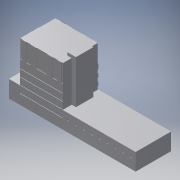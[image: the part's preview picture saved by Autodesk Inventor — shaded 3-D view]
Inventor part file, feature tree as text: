
AUTODESK INVENTOR PART (.ipt)
format: ipt  version: 2018.3 (Build 223284000, 284)  size: 415,744 bytes
history: native  units: mm
features: extrude x17, sketch x17, pattern_linear x3
ambient origin geometry x8: Origin, YZ Plane, XZ Plane, XY Plane, X Axis, Y Axis, Z Axis, Center Point
bodies: Solid1 (feature_tree)
feature tree (37):
  extrude  "Extrusion1"  Depth=28.01mm
  extrude  "Extrusion2"  Depth=0.31mm
  extrude  "Extrusion3"  Depth=8.81mm
  extrude  "Extrusion4"  Depth=33.64mm
  extrude  "Extrusion5"  Depth=31.92mm TaperAngle=0.0deg
  pattern_linear  "Rectangular Pattern1"  Count1=9 Spacing1=6.25mm
  extrude  "Extrusion6"  Depth=33.96mm
  extrude  "Extrusion7"  Depth=3.13mm
  pattern_linear  "Rectangular Pattern2"  Spacing1=7.78mm  [1 undecoded]
  extrude  "Extrusion8"  Depth=0.31mm TaperAngle=0.0deg
  extrude  "Extrusion9"  Depth=0.31mm TaperAngle=0.0deg
  extrude  "Extrusion10"  Depth=6.25mm
  extrude  "Extrusion11"  Depth=0.31mm TaperAngle=0.0deg
  pattern_linear  "Rectangular Pattern3"  Spacing1=5.26mm  [1 undecoded]
  extrude  "Extrusion12"  Depth=26.61mm
  extrude  "Extrusion13"  Depth=2.59mm
  extrude  "Extrusion14"  Depth=2.09mm
  extrude  "Extrusion15"  Depth=1.25mm TaperAngle=0.0deg
  extrude  "Extrusion16"  Depth=1.24mm TaperAngle=0.0deg
  extrude  "Extrusion17"  Depth=3.13mm
  sketch  "Sketch1"  dims[d0=100.0mm d1=28.01mm]
  sketch  "Sketch2"  dims[d2=13.41mm d3=0.0mm d4=0.31mm]
  sketch  "Sketch3"  dims[d5=0.31mm d6=8.81mm]
  sketch  "Sketch4"  dims[d7=57.55mm d8=33.64mm]
  sketch  "Sketch5"  dims[d9=27.39mm d10=31.92mm d11=0.0mm]
  sketch  "Sketch6"  dims[d12=6.8mm]
  sketch  "Sketch7"  dims[d13=6.8mm]
  sketch  "Sketch8"  dims[d14=3.35mm]
  sketch  "Sketch9"  dims[d15=34.21mm d16=0.0mm]
  sketch  "Sketch10"  dims[d17=3.44mm d18=0.0mm]
  sketch  "Sketch11"  dims[d19=2.5mm]
  sketch  "Sketch12"  dims[d20=1.25mm]
  sketch  "Sketch13"  dims[d21=1.25mm]
  sketch  "Sketch14"  dims[d22=3.13mm]
  sketch  "Sketch15"  dims[d23=2.95mm]
  sketch  "Sketch16"  dims[d24=0.31mm d25=0.0mm d26=90.0mm d28=6.25mm]
  sketch  "Sketch17"  dims[d29=3.35mm d30=33.96mm d31=3.13mm d32=7.78mm d33=0.31mm d34=0.0mm d35=0.31mm d36=0.0mm d37=90.0mm d39=6.25mm d40=0.31mm d41=0.0mm d42=5.26mm d43=26.61mm d44=2.59mm d45=2.09mm d46=1.25mm d47=0.0mm d48=1.24mm d49=0.0mm d50=3.13mm d51=2.5mm d52=0.31mm d53=0.0mm d54=20.0mm d56=5.63mm d57=4.07mm d58=2.5mm d59=0.31mm d60=0.0mm d61=3.1mm d62=4.61mm d63=4.61mm d64=3.1mm d65=14.1mm d66=0.0mm d67=0.31mm d68=0.0mm d69=0.31mm d70=0.0mm d71=0.31mm d72=0.0mm d73=4.38mm d74=4.38mm d75=4.38mm d76=12.39mm d77=0.7mm d78=0.7mm d79=0.31mm d80=0.0mm]
note: 2 required parameter values undecoded (feature->parameter linkage not recoverable at this tier; creation-order binding heuristic only, values carry confidence <= 0.55)
